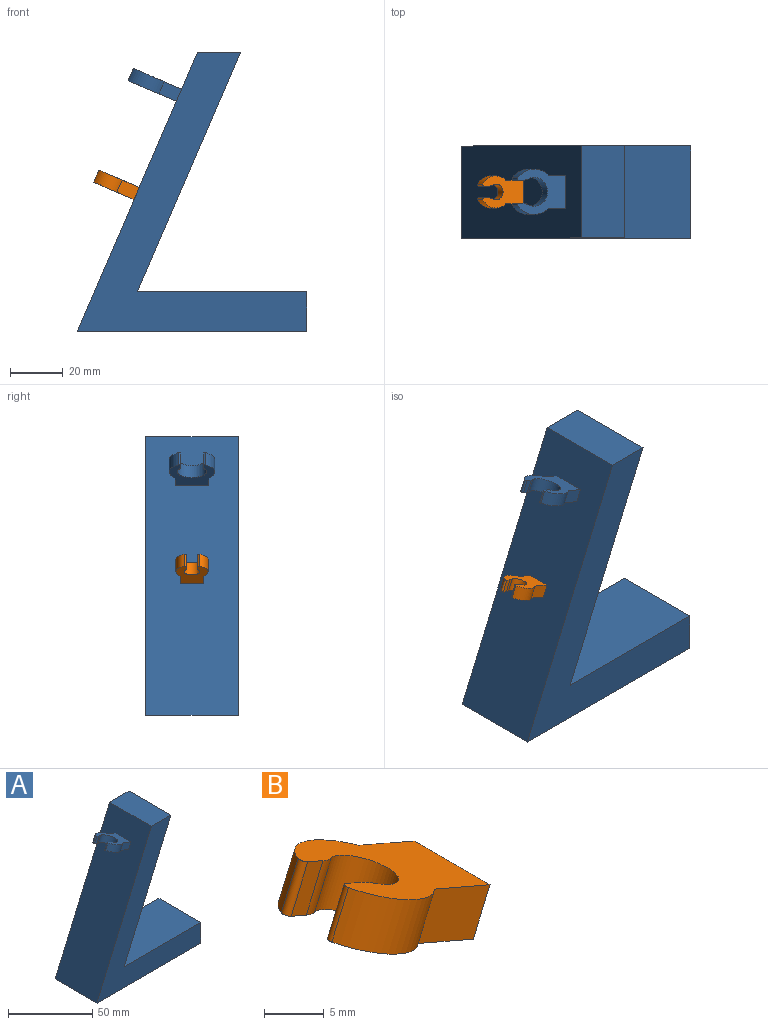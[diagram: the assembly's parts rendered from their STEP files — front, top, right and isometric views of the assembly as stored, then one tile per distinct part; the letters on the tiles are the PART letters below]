
ASSEMBLY  parts=2 mates=1
PART A: 21 faces, bbox 87x35x105.6 mm
  f0: plane 105.59x45.56mm, normal (-0.92,0,0.4), area 3961.7mm2, adj f1,f5,f6,f7,f12,f13,f19,f20
  f1: plane 87x35mm, normal (0,0,-1), area 3045mm2, adj f0,f2,f6,f7
  f2: plane 35x15mm, normal (1,0,0), area 525mm2, adj f1,f3,f6,f7
  f3: plane 64.19x35mm, normal (0,0,1), area 2246.7mm2, adj f2,f4,f6,f7
  f4: plane 90.59x39.09mm, normal (0.92,0,-0.4), area 3453.2mm2, adj f3,f5,f6,f7
  f5: plane 35x16.34mm, normal (0,0,1), area 571.8mm2, adj f0,f4,f6,f7
  f6: plane 105.59x87mm, normal (0,-1,0), area 2736.4mm2, adj f0,f1,f2,f3,f4,f5
  f7: plane 105.59x87mm, normal (0,1,0), area 2736.4mm2, adj f0,f1,f2,f3,f4,f5
  f8: cylinder r=3mm len=5.17mm, axis (0.4,0,0.92), area 7.6mm2, adj f9,f18,f19,f20
  f9: plane 5.5x4.08mm, normal (0,1,0), area 11.4mm2, adj f8,f10,f19,f20
  f10: cylinder r=0.5mm len=4.79mm, axis (0.4,0,0.92), area 5.6mm2, adj f9,f11,f19,f20
  f11: cylinder r=8.6mm len=13.6mm, axis (0.4,0,0.92), area 71.4mm2, adj f10,f12,f19,f20
  f12: plane 8.56x7.43mm, normal (0,-1,0), area 35.8mm2, adj f0,f11,f19,f20
  f13: plane 8.56x7.43mm, normal (0,1,0), area 35.8mm2, adj f0,f14,f19,f20
  f14: cylinder r=8.6mm len=13.6mm, axis (0.4,0,0.92), area 71.4mm2, adj f13,f15,f19,f20
  f15: cylinder r=0.5mm len=4.79mm, axis (0.4,0,0.92), area 5.6mm2, adj f14,f16,f19,f20
  f16: plane 5.5x4.08mm, normal (0,-1,0), area 11.4mm2, adj f15,f17,f19,f20
  f17: cylinder r=3mm len=5.17mm, axis (0.4,0,0.92), area 7.6mm2, adj f16,f18,f19,f20
  f18: cylinder r=5.5mm len=11mm, axis (0.4,0,0.92), area 114.4mm2, adj f8,f17,f19,f20
  f19: plane 18.29x17.2mm, normal (-0.4,0,-0.92), area 173.3mm2, adj f0,f8,f9,f10,f11,f12,f13,f14
  f20: plane 18.29x17.2mm, normal (0.4,0,0.92), area 173.3mm2, adj f0,f8,f9,f10,f11,f12,f13,f14
PART B: 14 faces, bbox 17.3x12.2x11.2 mm
  f0: cylinder r=3mm len=5.17mm, axis (-0.4,0,-0.92), area 7.6mm2, adj f1,f11,f12,f13
  f1: plane 5.37x3.78mm, normal (0,1,0), area 9.8mm2, adj f0,f2,f12,f13
  f2: cylinder r=0.5mm len=4.79mm, axis (-0.4,0,-0.92), area 5.2mm2, adj f1,f3,f12,f13
  f3: cylinder r=6.1mm len=10.66mm, axis (-0.4,0,-0.92), area 55mm2, adj f2,f4,f12,f13
  f4: plane 8.56x7.43mm, normal (0,-1,0), area 35.8mm2, adj f3,f5,f12,f13
  f5: plane 8.97x4.59mm, normal (0.92,0,-0.4), area 44.9mm2, adj f4,f6,f12,f13
  f6: plane 8.56x7.43mm, normal (0,1,0), area 35.8mm2, adj f5,f7,f12,f13
  f7: cylinder r=6.1mm len=10.66mm, axis (-0.4,0,-0.92), area 55mm2, adj f6,f8,f12,f13
  f8: cylinder r=0.5mm len=4.79mm, axis (-0.4,0,-0.92), area 5.2mm2, adj f7,f9,f12,f13
  f9: plane 5.37x3.78mm, normal (0,-1,0), area 9.8mm2, adj f8,f10,f12,f13
  f10: cylinder r=3mm len=5.17mm, axis (-0.4,0,-0.92), area 7.6mm2, adj f9,f11,f12,f13
  f11: cylinder r=3mm len=6.36mm, axis (-0.4,0,-0.92), area 62.4mm2, adj f0,f10,f12,f13
  f12: plane 15.31x12.2mm, normal (0.4,0,0.92), area 125.6mm2, adj f0,f1,f2,f3,f4,f5,f6,f7
  f13: plane 15.31x12.2mm, normal (-0.4,0,-0.92), area 125.6mm2, adj f0,f1,f2,f3,f4,f5,f6,f7
PLACE A at identity
PLACE B t=(-9.82,-15.45,-1.9)mm
MATE fastened B.f5 <-> A.f0  axis (0.92,0,-0.4) through (-9.07,-17.5,9.27)mm
